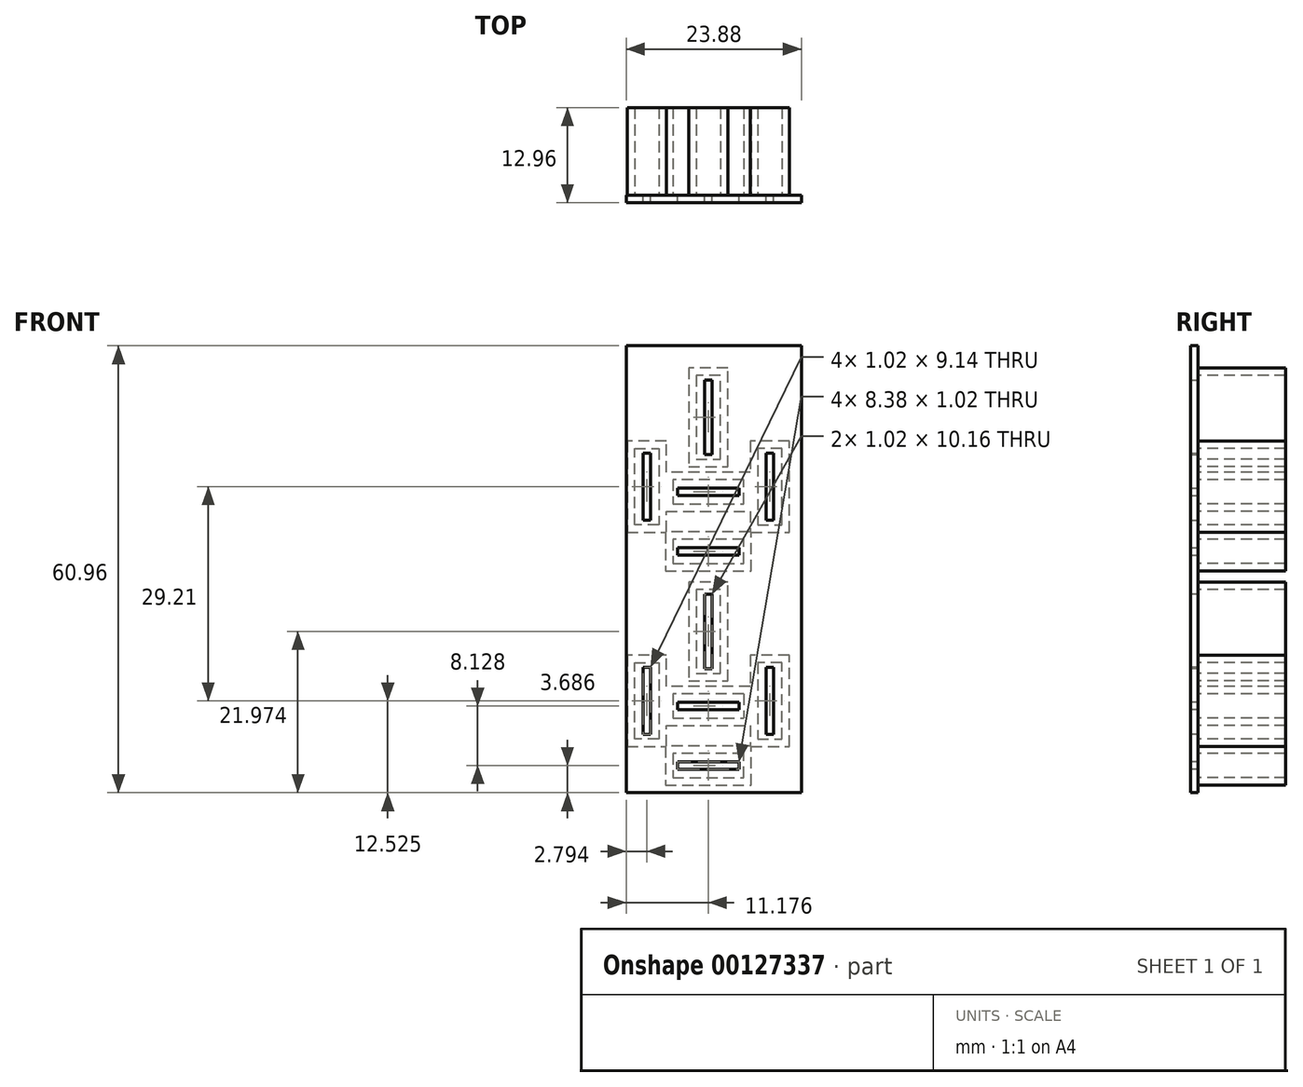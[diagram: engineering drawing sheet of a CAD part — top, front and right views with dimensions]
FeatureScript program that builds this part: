
annotation { "Feature Type Name" : "Feature", "Feature Type Description" : "" }
export const myFeature = defineFeature(function(context is Context, id is Id, definition is map)
    precondition{}
    {
        {
            var Q0;
            Q0=qCreatedBy(makeId("Front.planeOp"),FACE);
            var sketch = newSketch(context, id + "F0", { "sketchPlane" : qUnion([Q0])});
            skLineSegment(sketch, "E0", {"start": v(-3.35, 4.3) * mm, "end": v(-3.35, -26.19) * mm});
            skLineSegment(sketch, "E1", {"start": v(-3.35, -26.19) * mm, "end": v(22.05, -26.19) * mm});
            skLineSegment(sketch, "E2", {"start": v(22.05, -26.19) * mm, "end": v(22.05, 4.3) * mm});
            skLineSegment(sketch, "E3", {"start": v(22.05, 4.3) * mm, "end": v(-3.35, 4.3) * mm});
            skSolve(sketch);
        }
        {
            var Q0;
            Q0 = qSketchRegion(id + "F0", true);
            extrude(context, id + "F1", {"entities" : qUnion([Q0]), "depth" : 1.02 * mm});
        }
        {
            var Q0;
            Q0=qCreatedBy(makeId("Front.planeOp"),FACE);
            var sketch = newSketch(context, id + "F2", { "sketchPlane" : qUnion([Q0])});
            skLineSegment(sketch, "E4", {"start": v(8.84, -0.4) * mm, "end": v(8.84, -10.57) * mm});
            skLineSegment(sketch, "E5", {"start": v(8.84, -10.57) * mm, "end": v(9.85, -10.57) * mm});
            skLineSegment(sketch, "E6", {"start": v(9.85, -10.57) * mm, "end": v(9.85, -0.4) * mm});
            skLineSegment(sketch, "E7", {"start": v(9.85, -0.4) * mm, "end": v(8.84, -0.4) * mm});
            skLineSegment(sketch, "E8", {"start": v(0.46, -10.36) * mm, "end": v(0.46, -19.5) * mm});
            skLineSegment(sketch, "E9", {"start": v(0.46, -19.5) * mm, "end": v(1.47, -19.5) * mm});
            skLineSegment(sketch, "E10", {"start": v(1.47, -19.5) * mm, "end": v(1.47, -10.36) * mm});
            skLineSegment(sketch, "E11", {"start": v(1.47, -10.36) * mm, "end": v(0.46, -10.36) * mm});
            skLineSegment(sketch, "E12", {"start": v(17.22, -10.36) * mm, "end": v(17.22, -19.5) * mm});
            skLineSegment(sketch, "E13", {"start": v(17.22, -19.5) * mm, "end": v(18.24, -19.5) * mm});
            skLineSegment(sketch, "E14", {"start": v(18.24, -19.5) * mm, "end": v(18.24, -10.36) * mm});
            skLineSegment(sketch, "E15", {"start": v(17.22, -10.36) * mm, "end": v(18.24, -10.36) * mm});
            skLineSegment(sketch, "E16", {"start": v(5.15, -15.14) * mm, "end": v(5.15, -16.15) * mm});
            skLineSegment(sketch, "E17", {"start": v(5.15, -16.15) * mm, "end": v(13.54, -16.15) * mm});
            skLineSegment(sketch, "E18", {"start": v(13.54, -16.15) * mm, "end": v(13.54, -15.14) * mm});
            skLineSegment(sketch, "E19", {"start": v(5.15, -15.14) * mm, "end": v(13.54, -15.14) * mm});
            skLineSegment(sketch, "E20", {"start": v(5.15, -24.28) * mm, "end": v(13.54, -24.28) * mm});
            skLineSegment(sketch, "E21", {"start": v(13.54, -24.28) * mm, "end": v(13.54, -23.27) * mm});
            skLineSegment(sketch, "E22", {"start": v(13.54, -23.27) * mm, "end": v(5.15, -23.27) * mm});
            skLineSegment(sketch, "E23", {"start": v(5.15, -23.27) * mm, "end": v(5.15, -24.28) * mm});
            skSolve(sketch);
        }
        {
            var Q0;
            Q0 = qSketchRegion(id + "F2", true);
            extrude(context, id + "F3", {"entities" : qUnion([Q0]), "operationType" : NewBodyOperationType.REMOVE, "endBound" : BoundingType.THROUGH_ALL, "depth" : 25.4 * mm});
        }
        {
            var Q0;
            Q0=makeQuery(id+"F1.opExtrude","CAP_FACE",FACE,{"disambiguationData":[OSD([sQuery(id+"F0.wireOp",EDGE,"E0"),sQuery(id+"F0.wireOp",EDGE,"E1"),sQuery(id+"F0.wireOp",EDGE,"E2"),sQuery(id+"F0.wireOp",EDGE,"E3")])],"isStart":false});
            var sketch = newSketch(context, id + "F4", { "sketchPlane" : qUnion([Q0])});
            skLineSegment(sketch, "E24", {"start": v(-3.35, -26.19) * mm, "end": v(-3.35, -56.67) * mm});
            skLineSegment(sketch, "E25", {"start": v(-3.35, -56.67) * mm, "end": v(22.05, -56.67) * mm});
            skLineSegment(sketch, "E26", {"start": v(22.05, -56.67) * mm, "end": v(22.05, -26.19) * mm});
            skLineSegment(sketch, "E27", {"start": v(-3.35, -26.19) * mm, "end": v(22.05, -26.19) * mm});
            skSolve(sketch);
        }
        {
            var Q0;
            Q0 = qSketchRegion(id + "F4", true);
            extrude(context, id + "F5", {"entities" : qUnion([Q0]), "operationType" : NewBodyOperationType.ADD, "oppositeDirection" : true, "depth" : 1.02 * mm});
        }
        {
            var Q0;
            Q0=makeQuery(id+"F5.boolean.opBoolean","MERGE",FACE,{"derivedFrom":[makeQuery(id+"F1.opExtrude","CAP_FACE",FACE,{"disambiguationData":[OSD([sQuery(id+"F0.wireOp",EDGE,"E0"),sQuery(id+"F0.wireOp",EDGE,"E1"),sQuery(id+"F0.wireOp",EDGE,"E2"),sQuery(id+"F0.wireOp",EDGE,"E3")])],"isStart":false}),makeQuery(id+"F5.opExtrude","CAP_FACE",FACE,{"disambiguationData":[OSD([sQuery(id+"F4.wireOp",EDGE,"E24"),sQuery(id+"F4.wireOp",EDGE,"E25"),sQuery(id+"F4.wireOp",EDGE,"E26"),sQuery(id+"F4.wireOp",EDGE,"E27")])],"isStart":true})]});
            var sketch = newSketch(context, id + "F6", { "sketchPlane" : qUnion([Q0])});
            skLineSegment(sketch, "E28", {"start": v(1.47, -10.36) * mm, "end": v(0.46, -10.36) * mm});
            skLineSegment(sketch, "E29", {"start": v(0.46, -10.36) * mm, "end": v(0.46, -19.5) * mm});
            skLineSegment(sketch, "E30", {"start": v(0.46, -19.5) * mm, "end": v(1.47, -19.5) * mm});
            skLineSegment(sketch, "E31", {"start": v(1.47, -19.5) * mm, "end": v(1.47, -10.36) * mm});
            skLineSegment(sketch, "E32", {"start": v(5.15, -15.14) * mm, "end": v(5.15, -16.15) * mm});
            skLineSegment(sketch, "E33", {"start": v(5.15, -16.15) * mm, "end": v(13.54, -16.15) * mm});
            skLineSegment(sketch, "E34", {"start": v(13.54, -16.15) * mm, "end": v(13.54, -15.14) * mm});
            skLineSegment(sketch, "E35", {"start": v(13.54, -15.14) * mm, "end": v(5.15, -15.14) * mm});
            skLineSegment(sketch, "E36", {"start": v(8.84, -10.57) * mm, "end": v(9.85, -10.57) * mm});
            skLineSegment(sketch, "E37", {"start": v(9.85, -10.57) * mm, "end": v(9.85, -0.4) * mm});
            skLineSegment(sketch, "E38", {"start": v(9.85, -0.4) * mm, "end": v(8.84, -0.4) * mm});
            skLineSegment(sketch, "E39", {"start": v(8.84, -0.4) * mm, "end": v(8.84, -10.57) * mm});
            skLineSegment(sketch, "E40", {"start": v(17.22, -10.36) * mm, "end": v(18.24, -10.36) * mm});
            skLineSegment(sketch, "E41", {"start": v(18.24, -10.36) * mm, "end": v(18.24, -19.5) * mm});
            skLineSegment(sketch, "E42", {"start": v(18.24, -19.5) * mm, "end": v(17.22, -19.5) * mm});
            skLineSegment(sketch, "E43", {"start": v(17.22, -19.5) * mm, "end": v(17.22, -10.36) * mm});
            skLineSegment(sketch, "E44", {"start": v(13.54, -23.27) * mm, "end": v(13.54, -24.28) * mm});
            skLineSegment(sketch, "E45", {"start": v(13.54, -24.28) * mm, "end": v(5.15, -24.28) * mm});
            skLineSegment(sketch, "E46", {"start": v(5.15, -24.28) * mm, "end": v(5.15, -23.27) * mm});
            skLineSegment(sketch, "E47", {"start": v(5.15, -23.27) * mm, "end": v(13.54, -23.27) * mm});
            skLineSegment(sketch, "E48.0.1.0", {"start": v(9.85, -39.78) * mm, "end": v(9.85, -29.62) * mm});
            skLineSegment(sketch, "E48.0.1.1", {"start": v(8.84, -29.62) * mm, "end": v(8.84, -39.78) * mm});
            skLineSegment(sketch, "E48.0.1.2", {"start": v(17.22, -48.72) * mm, "end": v(17.22, -39.57) * mm});
            skLineSegment(sketch, "E48.0.1.3", {"start": v(18.24, -39.57) * mm, "end": v(18.24, -48.72) * mm});
            skLineSegment(sketch, "E48.0.1.4", {"start": v(13.54, -44.35) * mm, "end": v(5.15, -44.35) * mm});
            skLineSegment(sketch, "E48.0.1.5", {"start": v(5.15, -45.36) * mm, "end": v(13.54, -45.36) * mm});
            skLineSegment(sketch, "E48.0.1.6", {"start": v(5.15, -52.48) * mm, "end": v(13.54, -52.48) * mm});
            skLineSegment(sketch, "E48.0.1.7", {"start": v(13.54, -53.5) * mm, "end": v(5.15, -53.5) * mm});
            skLineSegment(sketch, "E48.0.1.8", {"start": v(1.47, -48.72) * mm, "end": v(1.47, -39.57) * mm});
            skLineSegment(sketch, "E48.0.1.9", {"start": v(0.46, -39.57) * mm, "end": v(0.46, -48.72) * mm});
            skLineSegment(sketch, "E48.0.1.10", {"start": v(1.47, -39.57) * mm, "end": v(0.46, -39.57) * mm});
            skLineSegment(sketch, "E48.0.1.11", {"start": v(0.46, -48.72) * mm, "end": v(1.47, -48.72) * mm});
            skLineSegment(sketch, "E48.0.1.12", {"start": v(5.15, -44.35) * mm, "end": v(5.15, -45.36) * mm});
            skLineSegment(sketch, "E48.0.1.13", {"start": v(13.54, -45.36) * mm, "end": v(13.54, -44.35) * mm});
            skLineSegment(sketch, "E48.0.1.14", {"start": v(17.22, -39.57) * mm, "end": v(18.24, -39.57) * mm});
            skLineSegment(sketch, "E48.0.1.15", {"start": v(18.24, -48.72) * mm, "end": v(17.22, -48.72) * mm});
            skLineSegment(sketch, "E48.0.1.16", {"start": v(8.84, -39.78) * mm, "end": v(9.85, -39.78) * mm});
            skLineSegment(sketch, "E48.0.1.17", {"start": v(9.85, -29.62) * mm, "end": v(8.84, -29.62) * mm});
            skLineSegment(sketch, "E48.0.1.18", {"start": v(5.15, -53.5) * mm, "end": v(5.15, -52.48) * mm});
            skLineSegment(sketch, "E48.0.1.19", {"start": v(13.54, -52.48) * mm, "end": v(13.54, -53.5) * mm});
            skLineSegment(sketch, "E48.direction1", {"start": v(9.85, -10.57) * mm, "end": v(35.25, -10.57) * mm, "construction": true});
            skLineSegment(sketch, "E48.direction2", {"start": v(9.85, -10.57) * mm, "end": v(9.85, -39.78) * mm, "construction": true});
            skSolve(sketch);
        }
        {
            var Q0;
            Q0 = qSketchRegion(id + "F6", true);
            extrude(context, id + "F7", {"entities" : qUnion([Q0]), "operationType" : NewBodyOperationType.REMOVE, "endBound" : BoundingType.THROUGH_ALL, "oppositeDirection" : true, "depth" : 25.4 * mm});
        }
        {
            var Q0;
            Q0=makeQuery(id+"F5.boolean.opBoolean","MERGE",FACE,{"derivedFrom":[makeQuery(id+"F1.opExtrude","CAP_FACE",FACE,{"disambiguationData":[OSD([sQuery(id+"F0.wireOp",EDGE,"E0"),sQuery(id+"F0.wireOp",EDGE,"E1"),sQuery(id+"F0.wireOp",EDGE,"E2"),sQuery(id+"F0.wireOp",EDGE,"E3")])],"isStart":false}),makeQuery(id+"F5.opExtrude","CAP_FACE",FACE,{"disambiguationData":[OSD([sQuery(id+"F4.wireOp",EDGE,"E24"),sQuery(id+"F4.wireOp",EDGE,"E25"),sQuery(id+"F4.wireOp",EDGE,"E26"),sQuery(id+"F4.wireOp",EDGE,"E27")])],"isStart":true})]});
            var sketch = newSketch(context, id + "F8", { "sketchPlane" : qUnion([Q0])});
            skLineSegment(sketch, "E49", {"start": v(11, 0.23) * mm, "end": v(7.7, 0.23) * mm});
            skLineSegment(sketch, "E50", {"start": v(7.7, 0.23) * mm, "end": v(7.7, -11.2) * mm});
            skLineSegment(sketch, "E51", {"start": v(7.7, -11.2) * mm, "end": v(11, -11.2) * mm});
            skLineSegment(sketch, "E52", {"start": v(11, -11.2) * mm, "end": v(11, 0.23) * mm});
            skLineSegment(sketch, "E53", {"start": v(-0.69, -9.73) * mm, "end": v(2.61, -9.73) * mm});
            skLineSegment(sketch, "E54", {"start": v(2.61, -9.73) * mm, "end": v(2.61, -20.14) * mm});
            skLineSegment(sketch, "E55", {"start": v(2.61, -20.14) * mm, "end": v(-0.69, -20.14) * mm});
            skLineSegment(sketch, "E56", {"start": v(-0.69, -20.14) * mm, "end": v(-0.69, -9.73) * mm});
            skLineSegment(sketch, "E57", {"start": v(4.52, -22.12) * mm, "end": v(4.52, -25.43) * mm});
            skLineSegment(sketch, "E58", {"start": v(4.52, -25.43) * mm, "end": v(14.17, -25.43) * mm});
            skLineSegment(sketch, "E59", {"start": v(14.17, -25.43) * mm, "end": v(14.17, -22.12) * mm});
            skLineSegment(sketch, "E60", {"start": v(14.17, -22.12) * mm, "end": v(4.52, -22.12) * mm});
            skLineSegment(sketch, "E61", {"start": v(16.08, -9.73) * mm, "end": v(16.08, -20.14) * mm});
            skLineSegment(sketch, "E62", {"start": v(16.08, -20.14) * mm, "end": v(19.38, -20.14) * mm});
            skLineSegment(sketch, "E63", {"start": v(19.38, -20.14) * mm, "end": v(19.38, -9.73) * mm});
            skLineSegment(sketch, "E64", {"start": v(19.38, -9.73) * mm, "end": v(16.08, -9.73) * mm});
            skLineSegment(sketch, "E65", {"start": v(4.52, -14) * mm, "end": v(4.52, -17.3) * mm});
            skLineSegment(sketch, "E66", {"start": v(4.52, -17.3) * mm, "end": v(14.17, -17.3) * mm});
            skLineSegment(sketch, "E67", {"start": v(14.17, -17.3) * mm, "end": v(14.17, -14) * mm});
            skLineSegment(sketch, "E68", {"start": v(14.17, -14) * mm, "end": v(4.52, -14) * mm});
            skLineSegment(sketch, "E69", {"start": v(6.68, 1.24) * mm, "end": v(6.68, -12.22) * mm});
            skLineSegment(sketch, "E70", {"start": v(6.68, -12.22) * mm, "end": v(12.01, -12.22) * mm});
            skLineSegment(sketch, "E71", {"start": v(12.01, -12.22) * mm, "end": v(12.01, 1.24) * mm});
            skLineSegment(sketch, "E72", {"start": v(12.01, 1.24) * mm, "end": v(6.68, 1.24) * mm});
            skLineSegment(sketch, "E73", {"start": v(3.63, -8.71) * mm, "end": v(-1.7, -8.71) * mm});
            skLineSegment(sketch, "E74", {"start": v(-1.7, -8.71) * mm, "end": v(-1.7, -21.16) * mm});
            skLineSegment(sketch, "E75", {"start": v(-1.7, -21.16) * mm, "end": v(3.63, -21.16) * mm});
            skLineSegment(sketch, "E76", {"start": v(3.63, -21.16) * mm, "end": v(3.63, -8.71) * mm});
            skLineSegment(sketch, "E77", {"start": v(3.5, -21.1) * mm, "end": v(3.5, -26.44) * mm});
            skLineSegment(sketch, "E78", {"start": v(3.5, -26.44) * mm, "end": v(15.19, -26.44) * mm});
            skLineSegment(sketch, "E79", {"start": v(15.19, -26.44) * mm, "end": v(15.19, -21.1) * mm});
            skLineSegment(sketch, "E80", {"start": v(15.19, -21.1) * mm, "end": v(3.5, -21.1) * mm});
            skLineSegment(sketch, "E81", {"start": v(15.06, -8.71) * mm, "end": v(15.06, -21.16) * mm});
            skLineSegment(sketch, "E82", {"start": v(15.06, -21.16) * mm, "end": v(20.4, -21.16) * mm});
            skLineSegment(sketch, "E83", {"start": v(20.4, -21.16) * mm, "end": v(20.4, -8.71) * mm});
            skLineSegment(sketch, "E84", {"start": v(20.4, -8.71) * mm, "end": v(15.06, -8.71) * mm});
            skLineSegment(sketch, "E85", {"start": v(3.5, -12.98) * mm, "end": v(3.5, -18.31) * mm});
            skLineSegment(sketch, "E86", {"start": v(3.5, -18.31) * mm, "end": v(15.19, -18.31) * mm});
            skLineSegment(sketch, "E87", {"start": v(15.19, -18.31) * mm, "end": v(15.19, -12.98) * mm});
            skLineSegment(sketch, "E88", {"start": v(15.19, -12.98) * mm, "end": v(3.5, -12.98) * mm});
            skLineSegment(sketch, "E89.0.1.0", {"start": v(12.01, -27.97) * mm, "end": v(6.68, -27.97) * mm});
            skLineSegment(sketch, "E89.0.1.1", {"start": v(11, -28.98) * mm, "end": v(7.7, -28.98) * mm});
            skLineSegment(sketch, "E89.0.1.2", {"start": v(6.68, -27.97) * mm, "end": v(6.68, -41.43) * mm});
            skLineSegment(sketch, "E89.0.1.3", {"start": v(12.01, -41.43) * mm, "end": v(12.01, -27.97) * mm});
            skLineSegment(sketch, "E89.0.1.4", {"start": v(11, -40.41) * mm, "end": v(11, -28.98) * mm});
            skLineSegment(sketch, "E89.0.1.5", {"start": v(7.7, -28.98) * mm, "end": v(7.7, -40.41) * mm});
            skLineSegment(sketch, "E89.0.1.6", {"start": v(7.7, -40.41) * mm, "end": v(11, -40.41) * mm});
            skLineSegment(sketch, "E89.0.1.7", {"start": v(6.68, -41.43) * mm, "end": v(12.01, -41.43) * mm});
            skLineSegment(sketch, "E89.0.1.8", {"start": v(16.08, -38.94) * mm, "end": v(16.08, -49.35) * mm});
            skLineSegment(sketch, "E89.0.1.9", {"start": v(15.06, -37.92) * mm, "end": v(15.06, -50.37) * mm});
            skLineSegment(sketch, "E89.0.1.10", {"start": v(15.06, -50.37) * mm, "end": v(20.4, -50.37) * mm});
            skLineSegment(sketch, "E89.0.1.11", {"start": v(16.08, -49.35) * mm, "end": v(19.38, -49.35) * mm});
            skLineSegment(sketch, "E89.0.1.12", {"start": v(20.4, -50.37) * mm, "end": v(20.4, -37.92) * mm});
            skLineSegment(sketch, "E89.0.1.13", {"start": v(19.38, -49.35) * mm, "end": v(19.38, -38.94) * mm});
            skLineSegment(sketch, "E89.0.1.14", {"start": v(19.38, -38.94) * mm, "end": v(16.08, -38.94) * mm});
            skLineSegment(sketch, "E89.0.1.15", {"start": v(20.4, -37.92) * mm, "end": v(15.06, -37.92) * mm});
            skLineSegment(sketch, "E89.0.1.16", {"start": v(15.19, -42.19) * mm, "end": v(3.5, -42.19) * mm});
            skLineSegment(sketch, "E89.0.1.17", {"start": v(14.17, -43.2) * mm, "end": v(4.52, -43.2) * mm});
            skLineSegment(sketch, "E89.0.1.18", {"start": v(4.52, -46.5) * mm, "end": v(14.17, -46.5) * mm});
            skLineSegment(sketch, "E89.0.1.19", {"start": v(3.5, -47.52) * mm, "end": v(15.19, -47.52) * mm});
            skLineSegment(sketch, "E89.0.1.20", {"start": v(3.5, -42.19) * mm, "end": v(3.5, -47.52) * mm});
            skLineSegment(sketch, "E89.0.1.21", {"start": v(4.52, -43.2) * mm, "end": v(4.52, -46.5) * mm});
            skLineSegment(sketch, "E89.0.1.22", {"start": v(2.61, -38.94) * mm, "end": v(2.61, -49.35) * mm});
            skLineSegment(sketch, "E89.0.1.23", {"start": v(3.63, -50.37) * mm, "end": v(3.63, -37.92) * mm});
            skLineSegment(sketch, "E89.0.1.24", {"start": v(3.63, -37.92) * mm, "end": v(-1.7, -37.92) * mm});
            skLineSegment(sketch, "E89.0.1.25", {"start": v(-1.7, -37.92) * mm, "end": v(-1.7, -50.37) * mm});
            skLineSegment(sketch, "E89.0.1.26", {"start": v(2.61, -49.35) * mm, "end": v(-0.69, -49.35) * mm});
            skLineSegment(sketch, "E89.0.1.27", {"start": v(-0.69, -49.35) * mm, "end": v(-0.69, -38.94) * mm});
            skLineSegment(sketch, "E89.0.1.28", {"start": v(-1.7, -50.37) * mm, "end": v(3.63, -50.37) * mm});
            skLineSegment(sketch, "E89.0.1.29", {"start": v(-0.69, -38.94) * mm, "end": v(2.61, -38.94) * mm});
            skLineSegment(sketch, "E89.0.1.30", {"start": v(15.19, -50.32) * mm, "end": v(3.5, -50.32) * mm});
            skLineSegment(sketch, "E89.0.1.31", {"start": v(14.17, -51.33) * mm, "end": v(4.52, -51.33) * mm});
            skLineSegment(sketch, "E89.0.1.32", {"start": v(3.5, -50.32) * mm, "end": v(3.5, -55.65) * mm});
            skLineSegment(sketch, "E89.0.1.33", {"start": v(4.52, -51.33) * mm, "end": v(4.52, -54.64) * mm});
            skLineSegment(sketch, "E89.0.1.34", {"start": v(3.5, -55.65) * mm, "end": v(15.19, -55.65) * mm});
            skLineSegment(sketch, "E89.0.1.35", {"start": v(4.52, -54.64) * mm, "end": v(14.17, -54.64) * mm});
            skLineSegment(sketch, "E89.0.1.36", {"start": v(14.17, -54.64) * mm, "end": v(14.17, -51.33) * mm});
            skLineSegment(sketch, "E89.0.1.37", {"start": v(15.19, -55.65) * mm, "end": v(15.19, -50.32) * mm});
            skLineSegment(sketch, "E89.direction1", {"start": v(6.68, 1.24) * mm, "end": v(32.08, 1.24) * mm, "construction": true});
            skLineSegment(sketch, "E89.direction2", {"start": v(6.68, 1.24) * mm, "end": v(6.68, -27.97) * mm, "construction": true});
            skLineSegment(sketch, "E90", {"start": v(14.17, -43.2) * mm, "end": v(14.17, -46.5) * mm});
            skLineSegment(sketch, "E91", {"start": v(15.19, -42.19) * mm, "end": v(15.19, -47.52) * mm});
            skSolve(sketch);
        }
        {
            var Q0;
            Q0 = qSketchRegion(id + "F8", true);
            extrude(context, id + "F9", {"entities" : qUnion([Q0]), "operationType" : NewBodyOperationType.ADD, "oppositeDirection" : true, "depth" : 12.95 * mm});
        }
        {
            var Q0;
            Q0=makeQuery(id+"F5.boolean.opBoolean","MERGE",FACE,{"derivedFrom":[makeQuery(id+"F1.opExtrude","CAP_FACE",FACE,{"disambiguationData":[OSD([sQuery(id+"F0.wireOp",EDGE,"E0"),sQuery(id+"F0.wireOp",EDGE,"E1"),sQuery(id+"F0.wireOp",EDGE,"E2"),sQuery(id+"F0.wireOp",EDGE,"E3")])],"isStart":false}),makeQuery(id+"F5.opExtrude","CAP_FACE",FACE,{"disambiguationData":[OSD([sQuery(id+"F4.wireOp",EDGE,"E24"),sQuery(id+"F4.wireOp",EDGE,"E25"),sQuery(id+"F4.wireOp",EDGE,"E26"),sQuery(id+"F4.wireOp",EDGE,"E27")])],"isStart":true})]});
            var sketch = newSketch(context, id + "F10", { "sketchPlane" : qUnion([Q0])});
            skLineSegment(sketch, "E92", {"start": v(-3.35, 4.3) * mm, "end": v(-1.83, 4.3) * mm});
            skLineSegment(sketch, "E93", {"start": v(-1.83, 4.3) * mm, "end": v(-1.83, -56.67) * mm});
            skLineSegment(sketch, "E94", {"start": v(-1.83, -56.67) * mm, "end": v(-3.35, -56.67) * mm});
            skLineSegment(sketch, "E95", {"start": v(-3.35, -56.67) * mm, "end": v(-3.35, 4.3) * mm});
            skSolve(sketch);
        }
        {
            var Q0;
            Q0 = qSketchRegion(id + "F10", true);
            extrude(context, id + "F11", {"entities" : qUnion([Q0]), "operationType" : NewBodyOperationType.REMOVE, "oppositeDirection" : true, "depth" : 25.4 * mm});
        }
    });
